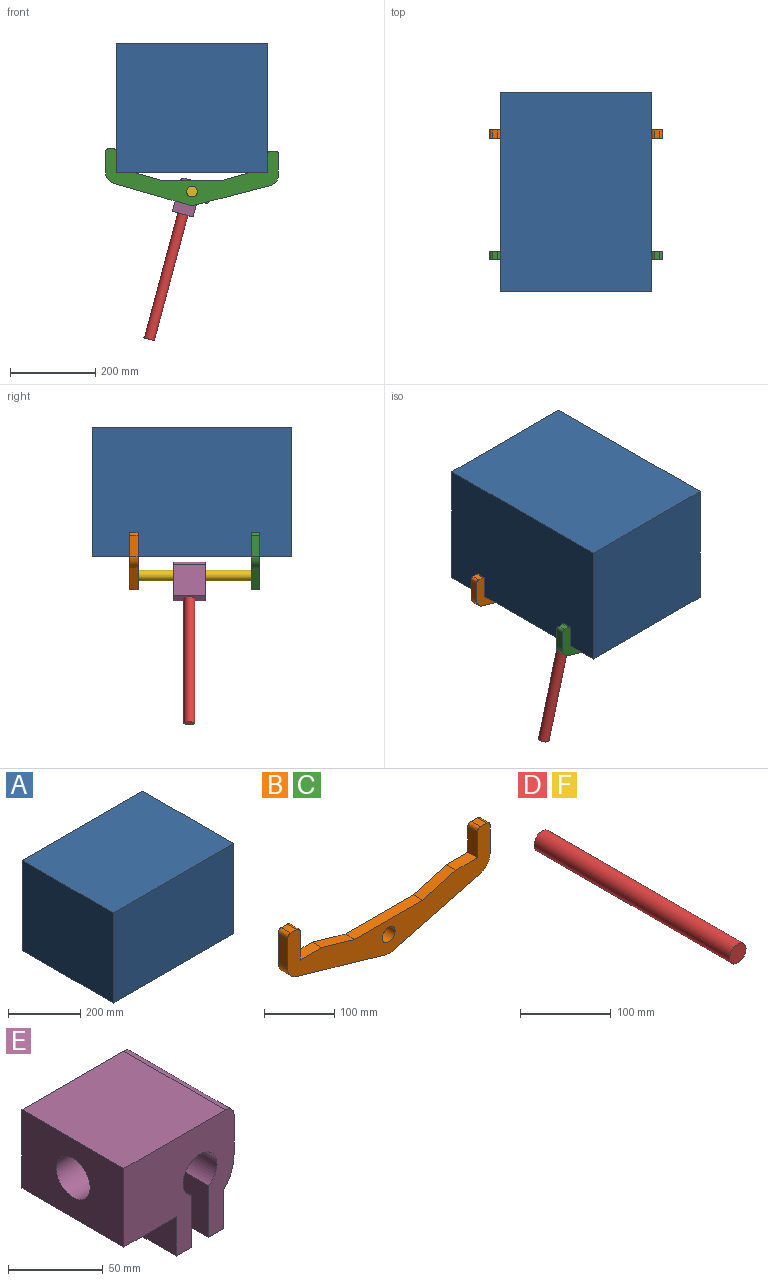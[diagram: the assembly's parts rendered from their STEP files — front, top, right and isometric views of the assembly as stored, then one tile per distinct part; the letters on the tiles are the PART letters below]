
ASSEMBLY  parts=6 mates=5
PART A: 8 faces, bbox 469.9x355.6x304.8 mm
  f0: plane 469.9x304.8mm, normal (0,1,0), area 143225.5mm2, adj f1,f3,f4,f5
  f1: plane 355.6x304.8mm, normal (-1,0,0), area 108386.9mm2, adj f0,f2,f4,f5
  f2: plane 469.9x304.8mm, normal (0,-1,0), area 143225.5mm2, adj f1,f3,f4,f5
  f3: plane 355.6x304.8mm, normal (1,0,0), area 108386.9mm2, adj f0,f2,f4,f5
  f4: plane 469.9x355.6mm, normal (0,0,1), area 167096.4mm2, adj f0,f1,f2,f3
  f5: plane 469.9x355.6mm, normal (0,0,-1), area 148855mm2, adj f0,f1,f2,f3,f6
  f6: cylinder r=76.2mm len=152.4mm, axis (0,0,-1), area 12161mm2, adj f5,f7
  f7: plane 152.4x152.4mm, normal (0,0,-1), area 18241.5mm2, adj f6
PART B: 23 faces, bbox 406.4x19.1x133.6 mm
  f0: plane 19.05x12.7mm, normal (0,0,1), area 241.9mm2, adj f1,f19,f21,f22
  f1: cylinder r=6.35mm len=19.05mm, axis (0,1,0), area 190mm2, adj f0,f2,f21,f22
  f2: plane 50.72x19.05mm, normal (-1,0,0), area 966.2mm2, adj f1,f3,f21,f22
  f3: cylinder r=25.4mm len=24.41mm, axis (0,1,0), area 624.7mm2, adj f2,f4,f21,f22
  f4: plane 178.13x51.16mm, normal (-0.28,0,-0.96), area 3530.6mm2, adj f3,f5,f21,f22
  f5: cylinder r=25.4mm len=19.05mm, axis (0,1,0), area 258.5mm2, adj f4,f6,f21,f22
  f6: plane 177.47x46.19mm, normal (0.25,0,-0.97), area 3493.5mm2, adj f5,f7,f21,f22
  f7: cylinder r=25.4mm len=24.58mm, axis (0,1,0), area 636.9mm2, adj f6,f8,f21,f22
  f8: plane 50.22x19.05mm, normal (1,0,0), area 956.6mm2, adj f7,f9,f21,f22
  f9: cylinder r=6.35mm len=19.05mm, axis (0,1,0), area 190mm2, adj f8,f10,f21,f22
  f10: plane 19.05x12.7mm, normal (0,0,1), area 241.9mm2, adj f9,f11,f21,f22
  f11: cylinder r=6.35mm len=19.05mm, axis (0,1,0), area 190mm2, adj f10,f12,f21,f22
  f12: plane 44.45x19.05mm, normal (-1,0,0), area 846.8mm2, adj f11,f13,f21,f22
  f13: plane 43.23x19.05mm, normal (0,0,1), area 823.6mm2, adj f12,f14,f21,f22
  f14: plane 66.26x19.05mm, normal (-0.28,0,0.96), area 1313.3mm2, adj f13,f15,f21,f22
  f15: plane 136.61x19.05mm, normal (0,0,1), area 2602.5mm2, adj f14,f16,f21,f22
  f16: plane 66.26x19.05mm, normal (0.28,0,0.96), area 1313.3mm2, adj f15,f17,f21,f22
  f17: plane 43.23x19.05mm, normal (0,0,1), area 823.6mm2, adj f16,f18,f21,f22
  f18: plane 49.92x19.05mm, normal (1,0,0), area 951mm2, adj f17,f19,f21,f22
  f19: cylinder r=6.35mm len=19.05mm, axis (0,1,0), area 190mm2, adj f0,f18,f21,f22
  f20: cylinder r=12.7mm len=25.4mm, axis (0,1,0), area 1520.1mm2, adj f21,f22
  f21: plane 406.4x133.63mm, normal (0,-1,0), area 18683.3mm2, adj f0,f1,f2,f3,f4,f5,f6,f7
  f22: plane 406.4x133.63mm, normal (0,1,0), area 18683.3mm2, adj f0,f1,f2,f3,f4,f5,f6,f7
PART C: same geometry as B
PART D: 3 faces, bbox 25.4x304.8x25.4 mm
  f0: cylinder r=12.7mm len=304.8mm, axis (0,1,0), area 24322mm2, adj f1,f2
  f1: plane 25.4x25.4mm, normal (0,-1,0), area 506.7mm2, adj f0
  f2: plane 25.4x25.4mm, normal (0,1,0), area 506.7mm2, adj f0
PART E: 17 faces, bbox 82.3x76.2x76.2 mm
  f0: plane 76.2x33.45mm, normal (-1,0,0), area 2549mm2, adj f1,f12,f13,f14
  f1: plane 76.2x11.43mm, normal (0,0,-1), area 871mm2, adj f0,f2,f13,f14
  f2: plane 76.2x25.4mm, normal (1,0,0), area 1935.5mm2, adj f1,f3,f13,f14
  f3: cylinder r=25.4mm len=76.2mm, axis (0,1,0), area 1608.9mm2, adj f2,f4,f13,f14
  f4: plane 76.2x25.4mm, normal (1,0,0), area 1935.5mm2, adj f3,f5,f13,f14
  f5: cylinder r=6.35mm len=76.2mm, axis (0,1,0), area 760.1mm2, adj f4,f6,f13,f14
  f6: plane 76.2x75.93mm, normal (0,0,1), area 5786mm2, adj f5,f7,f13,f14
  f7: plane 76.2x50.8mm, normal (-1,0,0), area 3364.3mm2, adj f6,f8,f13,f14,f15
  f8: plane 76.2x39.12mm, normal (0,0,-1), area 2980.8mm2, adj f7,f9,f13,f14
  f9: plane 76.2x25.4mm, normal (-1,0,0), area 1935.5mm2, adj f8,f10,f13,f14
  f10: plane 76.2x11.43mm, normal (0,0,-1), area 871mm2, adj f9,f11,f13,f14
  f11: plane 76.2x33.45mm, normal (1,0,0), area 2549mm2, adj f10,f12,f13,f14
  f12: cylinder r=12.7mm len=76.2mm, axis (0,1,0), area 5067.1mm2, adj f0,f11,f13,f14
  f13: plane 82.3x76.2mm, normal (0,-1,0), area 4114.9mm2, adj f0,f1,f2,f3,f4,f5,f6,f7
  f14: plane 82.3x76.2mm, normal (0,1,0), area 4114.9mm2, adj f0,f1,f2,f3,f4,f5,f6,f7
  f15: cylinder r=12.7mm len=38.1mm, axis (-1,0,0), area 3040.2mm2, adj f7,f16
  f16: plane 25.4x25.4mm, normal (-1,0,0), area 506.7mm2, adj f15
PART F: same geometry as D
PLACE A rot(axis=(0,0,-1),90deg) t=(0,-146.05,43.63)mm
PLACE B t=(0,0,19.03)mm
PLACE C t=(0,-285.75,19.03)mm
PLACE D rot(axis=(-0.52,-0.52,0.68),111.8deg) t=(-100.91,-139.84,-347.42)mm
PLACE E rot(axis=(0,-1,0),75deg) t=(-0.88,-101.6,0.24)mm
PLACE F at identity
MATE fastened F.f0 <-> C.f20  axis (0,-1,0) through (0,-304.8,0)mm
MATE fastened A.f3 <-> C.f3  axis (0,-1,0) through (-177.8,-381,43.63)mm
MATE fastened E.f15 <-> D.f0  axis (-0.26,0,-0.97) through (-22.02,-139.84,-53)mm
MATE fastened F.f0 <-> B.f20  axis (0,1,0) through (0,0,0)mm
MATE revolute F.f0 <-> E.f3  axis (0,1,0) through (0,-152.4,0)mm
